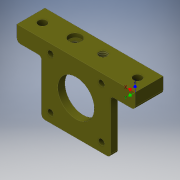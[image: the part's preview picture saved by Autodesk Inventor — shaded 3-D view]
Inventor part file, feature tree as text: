
AUTODESK INVENTOR PART (.ipt)
format: ipt  version: 2016 SP1 (Build 200210100, 210)  size: 340,480 bytes
history: native  units: in
note: dims shown in document units (in); Inventor stores cm internally (conversion verified against a paired STEP export)
features: sketch x10, other x3, plane x1
ambient origin geometry x8: Origin, YZ Plane, XZ Plane, XY Plane, X Axis, Y Axis, Z Axis, Center Point
bodies: Solid1 (feature_tree)
feature tree (14):
  other  "Part1.ipt"
  other  "Solid1::Part1.ipt"
  other  "TaggingFeature1"
  sketch  "Sketch1"  dims[d0=0.3937in]
  sketch  "Sketch2"
  sketch  "Sketch3"
  sketch  "Sketch4"
  sketch  "Sketch5"
  sketch  "Sketch6"
  sketch  "Sketch7"
  sketch  "Sketch8"
  sketch  "Sketch9"
  sketch  "Sketch10"
  plane  "Work Plane1"
